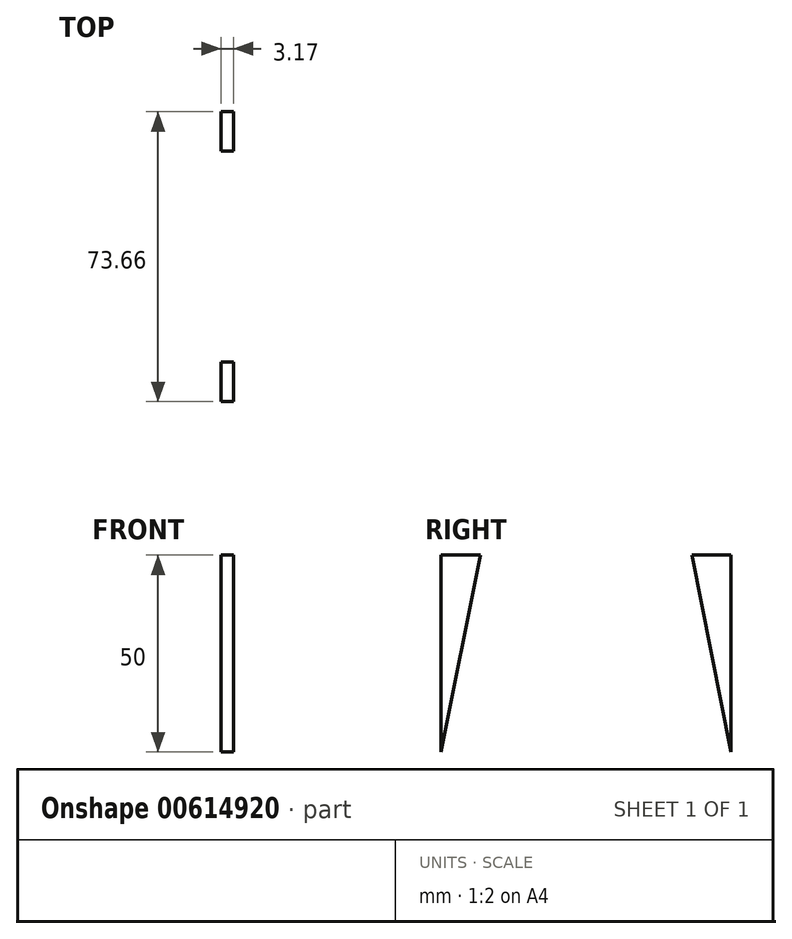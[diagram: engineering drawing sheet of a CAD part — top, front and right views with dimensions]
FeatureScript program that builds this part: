
annotation { "Feature Type Name" : "Feature", "Feature Type Description" : "" }
export const myFeature = defineFeature(function(context is Context, id is Id, definition is map)
    precondition{}
    {
        {
            var Q0;
            Q0=qCreatedBy(makeId("Right.planeOp"),FACE);
            var sketch = newSketch(context, id + "F0", { "sketchPlane" : qUnion([Q0])});
            skLineSegment(sketch, "E0.bottom", {"start": v(36.83, 25) * mm, "end": v(-36.82, 25) * mm});
            skLineSegment(sketch, "E0.top", {"start": v(36.83, -25) * mm, "end": v(-36.82, -25) * mm});
            skLineSegment(sketch, "E0.left", {"start": v(36.83, 25) * mm, "end": v(36.83, -25) * mm});
            skLineSegment(sketch, "E0.right", {"start": v(-36.82, 25) * mm, "end": v(-36.82, -25) * mm});
            skPoint(sketch, "E0.middle", {"position": v(0, 0) * mm});
            skLineSegment(sketch, "E1.bottom", {"start": v(36.83, 25) * mm, "end": v(26.83, 25) * mm});
            skLineSegment(sketch, "E1.top", {"start": v(36.83, 95) * mm, "end": v(26.83, 95) * mm});
            skLineSegment(sketch, "E1.left", {"start": v(36.83, 25) * mm, "end": v(36.83, 95) * mm});
            skLineSegment(sketch, "E1.right", {"start": v(26.83, 25) * mm, "end": v(26.83, 95) * mm});
            skLineSegment(sketch, "E2", {"start": v(26.83, 25) * mm, "end": v(36.83, -25) * mm});
            skLineSegment(sketch, "E3.MirrorCS", {"start": v(-26.83, 25) * mm, "end": v(-36.83, -25) * mm});
            skLineSegment(sketch, "E4.MirrorCS", {"start": v(-36.83, 25) * mm, "end": v(-26.83, 25) * mm});
            skLineSegment(sketch, "E5.MirrorCS", {"start": v(-36.83, 25) * mm, "end": v(-36.83, 95) * mm});
            skLineSegment(sketch, "E6.MirrorCS", {"start": v(-26.83, 25) * mm, "end": v(-26.83, 95) * mm});
            skLineSegment(sketch, "E7.MirrorCS", {"start": v(-36.83, 95) * mm, "end": v(-26.83, 95) * mm});
            skSolve(sketch);
        }
        {
            var Q0;
            Q0=makeQuery(id+"F0.imprint","IMPRINT",FACE,{"disambiguationData":[TD([[makeQuery(id+"F0.imprint","IMPRINT",EDGE,{"derivedFrom":sQuery(id+"F0.wireOp",EDGE,"E0.bottom")}),1.0]])]});
            var Q1;
            Q1=makeQuery(id+"F0.imprint","IMPRINT",FACE,{"disambiguationData":[TD([[makeQuery(id+"F0.imprint","IMPRINT",EDGE,{"derivedFrom":sQuery(id+"F0.wireOp",EDGE,"E1.bottom")}),-1.0]])]});
            var Q2;
            Q2=makeQuery(id+"F0.imprint","IMPRINT",FACE,{"disambiguationData":[TD([[makeQuery(id+"F0.imprint","IMPRINT",EDGE,{"derivedFrom":sQuery(id+"F0.wireOp",EDGE,"E0.left")}),1.0]])]});
            var Q3;
            Q3=makeQuery(id+"F0.imprint","IMPRINT",FACE,{"disambiguationData":[TD([[makeQuery(id+"F0.imprint","IMPRINT",EDGE,{"derivedFrom":sQuery(id+"F0.wireOp",EDGE,"E0.right")}),-1.0]])]});
            var Q4;
            Q4=makeQuery(id+"F0.imprint","IMPRINT",FACE,{"disambiguationData":[TD([[makeQuery(id+"F0.imprint","IMPRINT",EDGE,{"derivedFrom":sQuery(id+"F0.wireOp",EDGE,"E4.MirrorCS")}),1.0]])]});
            var Q5;
            Q5=makeQuery(id+"F0.imprint","IMPRINT",FACE,{"disambiguationData":[TD([[makeQuery(id+"F0.imprint","IMPRINT",EDGE,{"derivedFrom":sQuery(id+"F0.wireOp",EDGE,"E0.left")}),-1.0]])]});
            var Q6;
            Q6=makeQuery(id+"F0.imprint","IMPRINT",FACE,{"disambiguationData":[TD([[makeQuery(id+"F0.imprint","IMPRINT",EDGE,{"derivedFrom":sQuery(id+"F0.wireOp",EDGE,"E0.right")}),1.0]])]});
            extrude(context, id + "F1", {"entities" : qUnion([Q0, Q1, Q2, Q3, Q4, Q5, Q6]), "depth" : 3.17 * mm, "offsetDistance" : 25 * mm});
        }
    });
